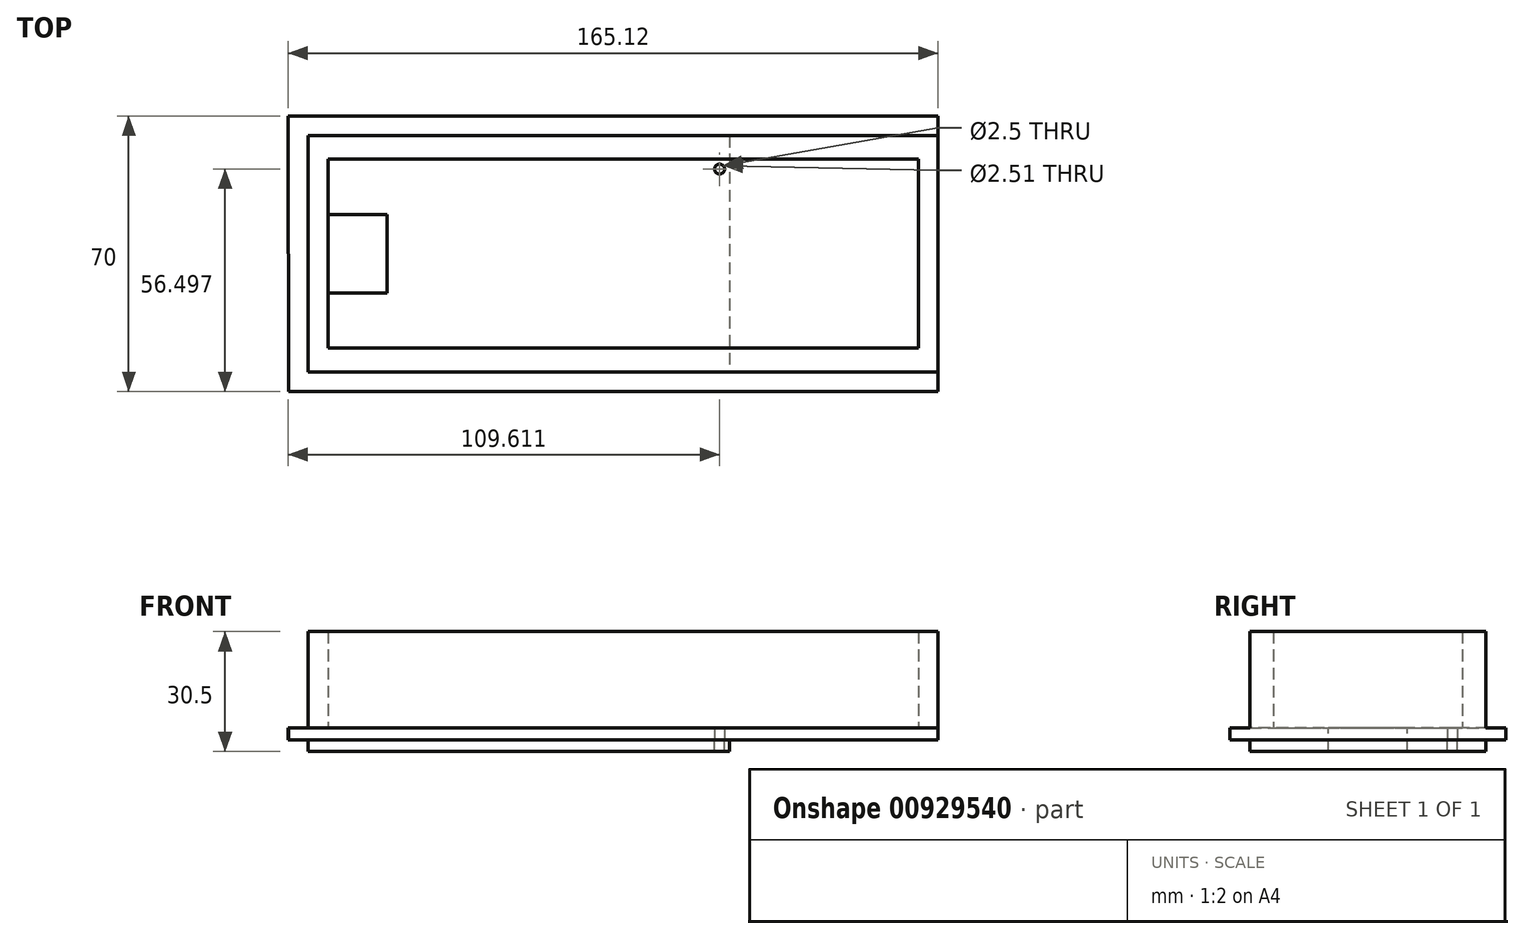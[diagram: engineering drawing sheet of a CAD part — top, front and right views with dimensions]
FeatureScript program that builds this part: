
annotation { "Feature Type Name" : "Feature", "Feature Type Description" : "" }
export const myFeature = defineFeature(function(context is Context, id is Id, definition is map)
    precondition{}
    {
        {
            var Q0;
            Q0=qCreatedBy(makeId("Top.planeOp"),FACE);
            var sketch = newSketch(context, id + "F0", { "sketchPlane" : qUnion([Q0])});
            skLineSegment(sketch, "E0.bottom", {"start": v(-59.45, 31.08) * mm, "end": v(47.55, 31.08) * mm});
            skLineSegment(sketch, "E0.top", {"start": v(-59.45, -28.92) * mm, "end": v(47.55, -28.92) * mm});
            skLineSegment(sketch, "E0.left", {"start": v(-59.45, 31.08) * mm, "end": v(-59.45, -28.92) * mm});
            skLineSegment(sketch, "E0.right", {"start": v(47.55, 31.08) * mm, "end": v(47.55, -28.92) * mm});
            skLineSegment(sketch, "E1.bottom", {"start": v(-54.45, 11.08) * mm, "end": v(-39.45, 11.08) * mm});
            skLineSegment(sketch, "E1.top", {"start": v(-54.45, -8.92) * mm, "end": v(-39.45, -8.92) * mm});
            skLineSegment(sketch, "E1.left", {"start": v(-54.45, 11.08) * mm, "end": v(-54.45, -8.92) * mm});
            skLineSegment(sketch, "E1.right", {"start": v(-39.45, 11.08) * mm, "end": v(-39.45, -8.92) * mm});
            skSolve(sketch);
        }
        {
            var Q0;
            Q0=makeQuery(id+"F0.imprint","IMPRINT",FACE,{"disambiguationData":[TD([[makeQuery(id+"F0.imprint","IMPRINT",EDGE,{"derivedFrom":sQuery(id+"F0.wireOp",EDGE,"E0.bottom")}),-1.0]])]});
            extrude(context, id + "F1", {"entities" : qUnion([Q0]), "oppositeDirection" : true, "depth" : 3 * mm, "offsetDistance" : 25 * mm});
        }
        {
            var Q0;
            Q0=qCreatedBy(makeId("Top.planeOp"),FACE);
            var sketch = newSketch(context, id + "F2", { "sketchPlane" : qUnion([Q0])});
            skLineSegment(sketch, "E2.top", {"start": v(-64.44, -33.92) * mm, "end": v(100.56, -33.92) * mm});
            skLineSegment(sketch, "E2.right", {"start": v(100.56, 36.08) * mm, "end": v(100.56, -33.92) * mm});
            skLineSegment(sketch, "E3.bottom", {"start": v(-54.45, 11.08) * mm, "end": v(-39.45, 11.08) * mm});
            skLineSegment(sketch, "E3.top", {"start": v(-54.45, -8.92) * mm, "end": v(-39.45, -8.92) * mm});
            skLineSegment(sketch, "E3.left", {"start": v(-54.45, 11.08) * mm, "end": v(-54.45, -8.92) * mm});
            skLineSegment(sketch, "E3.right", {"start": v(-39.45, 11.08) * mm, "end": v(-39.45, -8.92) * mm});
            skLineSegment(sketch, "E4", {"start": v(100.56, 36.08) * mm, "end": v(-64.56, 36.08) * mm});
            skLineSegment(sketch, "E5", {"start": v(-64.56, 36.08) * mm, "end": v(-64.44, -33.92) * mm});
            skSolve(sketch);
        }
        {
            var Q0;
            Q0=makeQuery(id+"F2.imprint","IMPRINT",FACE,{"disambiguationData":[TD([[makeQuery(id+"F2.imprint","IMPRINT",EDGE,{"derivedFrom":sQuery(id+"F2.wireOp",EDGE,"E2.top")}),1.0]])]});
            extrude(context, id + "F3", {"entities" : qUnion([Q0]), "operationType" : NewBodyOperationType.ADD, "depth" : 3 * mm, "offsetDistance" : 25 * mm});
        }
        {
            var Q0;
            Q0=qCreatedBy(makeId("Top.planeOp"),FACE);
            var sketch = newSketch(context, id + "F4", { "sketchPlane" : qUnion([Q0])});
            skLineSegment(sketch, "E6.bottom", {"start": v(-59.45, 31.08) * mm, "end": v(100.55, 31.08) * mm});
            skLineSegment(sketch, "E6.top", {"start": v(-59.45, -28.92) * mm, "end": v(100.55, -28.92) * mm});
            skLineSegment(sketch, "E6.left", {"start": v(-59.45, 31.08) * mm, "end": v(-59.45, -28.92) * mm});
            skLineSegment(sketch, "E6.right", {"start": v(100.55, 31.08) * mm, "end": v(100.55, -28.92) * mm});
            skLineSegment(sketch, "E7.bottom", {"start": v(-54.45, 25.08) * mm, "end": v(95.55, 25.08) * mm});
            skLineSegment(sketch, "E7.top", {"start": v(-54.45, -22.92) * mm, "end": v(95.55, -22.92) * mm});
            skLineSegment(sketch, "E7.left", {"start": v(-54.45, 25.08) * mm, "end": v(-54.45, -22.92) * mm});
            skLineSegment(sketch, "E7.right", {"start": v(95.55, 25.08) * mm, "end": v(95.55, -22.92) * mm});
            skPoint(sketch, "E8", {"position": v(45.05, 22.58) * mm});
            skSolve(sketch);
        }
        {
            var Q0;
            {var subQ1=sQuery(id+"F4.wireOp",EDGE,"E6.bottom");Q0=makeQuery(id+"F4.imprint","IMPRINT",FACE,{"disambiguationData":[TD([[makeQuery(id+"F4.imprint","IMPRINT",EDGE,{"derivedFrom":subQ1}),-1.0]])]});}
            extrude(context, id + "F5", {"entities" : qUnion([Q0]), "operationType" : NewBodyOperationType.ADD, "depth" : 27.5 * mm, "offsetDistance" : 25 * mm});
        }
        {
            var Q0;
            Q0=sQuery(id+"F4.wireOp",VERTEX,"E8");
            var Q1;
            Q1=makeQuery(id+"F1.opExtrude","SWEPT_BODY",BODY,{"disambiguationData":[OSD([sQuery(id+"F0.wireOp",EDGE,"E0.bottom"),sQuery(id+"F0.wireOp",EDGE,"E0.top"),sQuery(id+"F0.wireOp",EDGE,"E0.left"),sQuery(id+"F0.wireOp",EDGE,"E0.right"),sQuery(id+"F0.wireOp",EDGE,"E1.bottom"),sQuery(id+"F0.wireOp",EDGE,"E1.top"),sQuery(id+"F0.wireOp",EDGE,"E1.left"),sQuery(id+"F0.wireOp",EDGE,"E1.right")])]});
            hole(context, id + "F6", {"style" : HoleStyle.SIMPLE, "endStyle" : HoleEndStyle.THROUGH, "holeDiameter" : 2.5 * mm, "majorDiameter" : 5 * mm, "isTappedThrough" : true, "tappedDepth" : 12 * mm, "tapClearance" : 3, "locations" : qUnion([Q0]), "scope" : qUnion([Q1])});
        }
        {
            var Q0;
            Q0=sQuery(id+"F4.wireOp",VERTEX,"E8");
            var Q1;
            Q1=makeQuery(id+"F1.opExtrude","SWEPT_BODY",BODY,{"disambiguationData":[OSD([sQuery(id+"F0.wireOp",EDGE,"E0.bottom"),sQuery(id+"F0.wireOp",EDGE,"E0.top"),sQuery(id+"F0.wireOp",EDGE,"E0.left"),sQuery(id+"F0.wireOp",EDGE,"E0.right"),sQuery(id+"F0.wireOp",EDGE,"E1.bottom"),sQuery(id+"F0.wireOp",EDGE,"E1.top"),sQuery(id+"F0.wireOp",EDGE,"E1.left"),sQuery(id+"F0.wireOp",EDGE,"E1.right")])]});
            hole(context, id + "F7", {"style" : HoleStyle.SIMPLE, "endStyle" : HoleEndStyle.THROUGH, "oppositeDirection" : true, "holeDiameter" : 2.5 * mm, "majorDiameter" : 5 * mm, "isTappedThrough" : true, "tappedDepth" : 12 * mm, "tapClearance" : 3, "locations" : qUnion([Q0]), "scope" : qUnion([Q1])});
        }
    });
